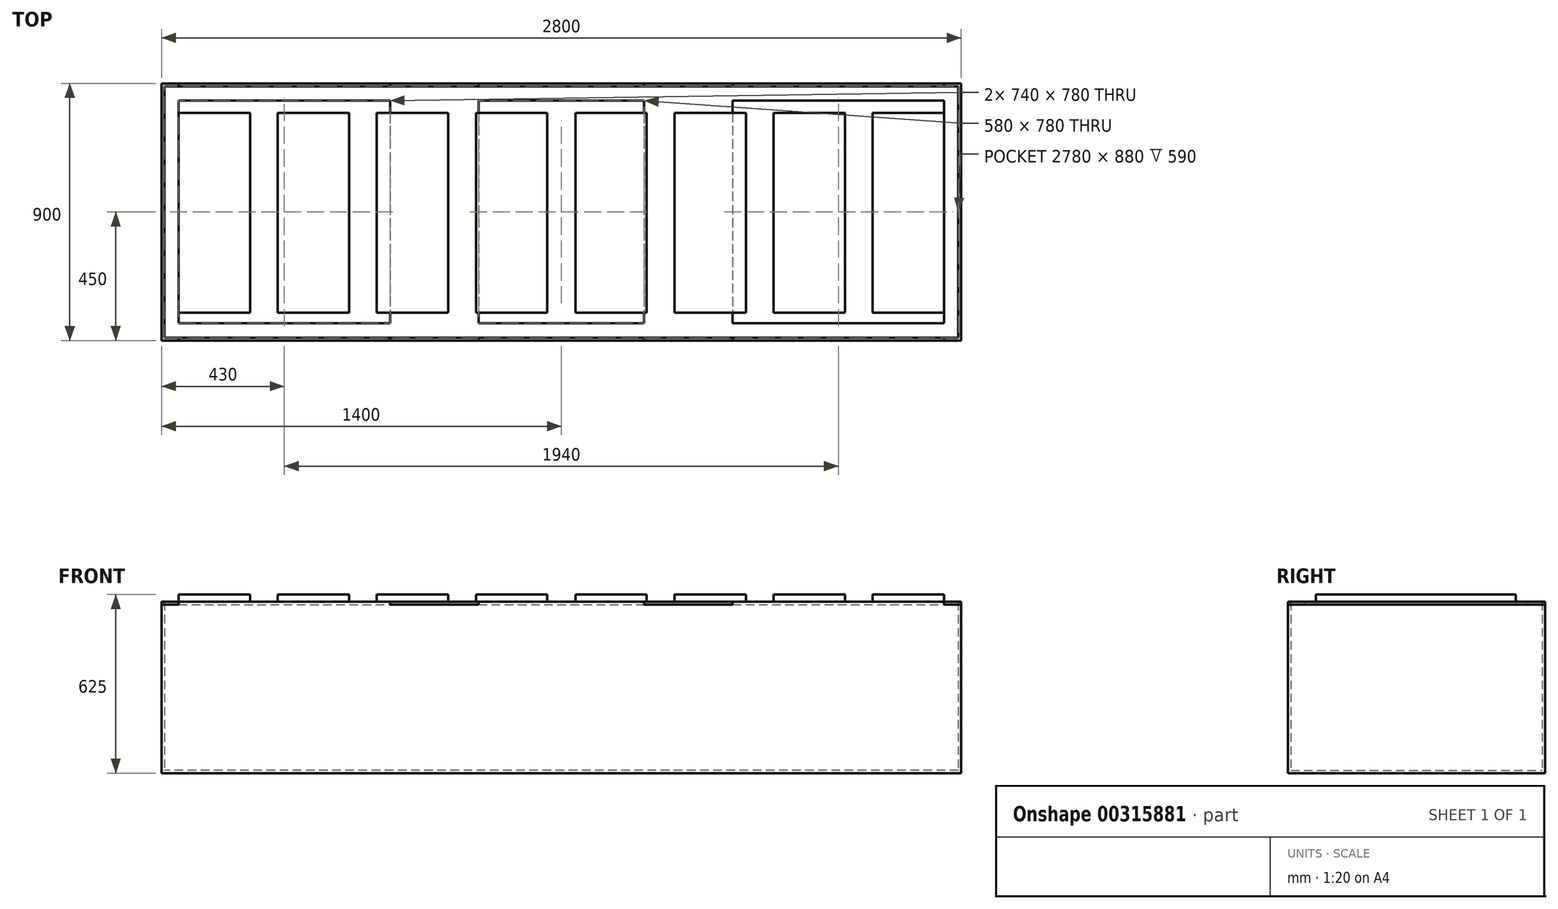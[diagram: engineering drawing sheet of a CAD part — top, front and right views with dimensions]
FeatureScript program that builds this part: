
annotation { "Feature Type Name" : "Feature", "Feature Type Description" : "" }
export const myFeature = defineFeature(function(context is Context, id is Id, definition is map)
    precondition{}
    {
        {
            var Q0;
            Q0=qCreatedBy(makeId("Top.planeOp"),FACE);
            var sketch = newSketch(context, id + "F0", { "sketchPlane" : qUnion([Q0])});
            skLineSegment(sketch, "E0.bottom", {"start": v(-1400, 450) * mm, "end": v(1400, 450) * mm});
            skLineSegment(sketch, "E0.top", {"start": v(-1400, -450) * mm, "end": v(1400, -450) * mm});
            skLineSegment(sketch, "E0.left", {"start": v(-1400, 450) * mm, "end": v(-1400, -450) * mm});
            skLineSegment(sketch, "E0.right", {"start": v(1400, 450) * mm, "end": v(1400, -450) * mm});
            skPoint(sketch, "E0.middle", {"position": v(0, 0) * mm});
            skLineSegment(sketch, "E1.bottom", {"start": v(-1390, 440) * mm, "end": v(1390, 440) * mm});
            skLineSegment(sketch, "E1.top", {"start": v(-1390, -440) * mm, "end": v(1390, -440) * mm});
            skLineSegment(sketch, "E1.left", {"start": v(-1390, 440) * mm, "end": v(-1390, -440) * mm});
            skLineSegment(sketch, "E1.right", {"start": v(1390, 440) * mm, "end": v(1390, -440) * mm});
            skSolve(sketch);
        }
        {
            var Q0;
            Q0=qSketchRegion(id+"F0",true);
            extrude(context, id + "F1", {"entities" : qUnion([Q0]), "depth" : 600 * mm});
        }
        {
            var Q0;
            Q0=makeQuery(id+"F1.opExtrude","CAP_FACE",FACE,{"disambiguationData":[OSD([sQuery(id+"F0.wireOp",EDGE,"E0.bottom"),sQuery(id+"F0.wireOp",EDGE,"E0.top"),sQuery(id+"F0.wireOp",EDGE,"E0.left"),sQuery(id+"F0.wireOp",EDGE,"E0.right"),sQuery(id+"F0.wireOp",EDGE,"E1.bottom"),sQuery(id+"F0.wireOp",EDGE,"E1.top"),sQuery(id+"F0.wireOp",EDGE,"E1.left"),sQuery(id+"F0.wireOp",EDGE,"E1.right")])],"isStart":true});
            var sketch = newSketch(context, id + "F2", { "sketchPlane" : qUnion([Q0])});
            skLineSegment(sketch, "E2.bottom", {"start": v(-1400, -450) * mm, "end": v(1400, -450) * mm});
            skLineSegment(sketch, "E2.top", {"start": v(-1400, 450) * mm, "end": v(1400, 450) * mm});
            skLineSegment(sketch, "E2.left", {"start": v(-1400, -450) * mm, "end": v(-1400, 450) * mm});
            skLineSegment(sketch, "E2.right", {"start": v(1400, -450) * mm, "end": v(1400, 450) * mm});
            skPoint(sketch, "E2.middle", {"position": v(0, 0) * mm});
            skSolve(sketch);
        }
        {
            var Q0;
            Q0=qSketchRegion(id+"F2",true);
            extrude(context, id + "F3", {"entities" : qUnion([Q0]), "operationType" : NewBodyOperationType.ADD, "oppositeDirection" : true, "depth" : 10 * mm});
        }
        {
            var Q0;
            Q0=makeQuery(id+"F1.opExtrude","CAP_FACE",FACE,{"disambiguationData":[OSD([sQuery(id+"F0.wireOp",EDGE,"E0.bottom"),sQuery(id+"F0.wireOp",EDGE,"E0.top"),sQuery(id+"F0.wireOp",EDGE,"E0.left"),sQuery(id+"F0.wireOp",EDGE,"E0.right"),sQuery(id+"F0.wireOp",EDGE,"E1.bottom"),sQuery(id+"F0.wireOp",EDGE,"E1.top"),sQuery(id+"F0.wireOp",EDGE,"E1.left"),sQuery(id+"F0.wireOp",EDGE,"E1.right")])],"isStart":false});
            var sketch = newSketch(context, id + "F4", { "sketchPlane" : qUnion([Q0])});
            skLineSegment(sketch, "E3.bottom", {"start": v(-1400, -450) * mm, "end": v(-1340, -450) * mm});
            skLineSegment(sketch, "E3.top", {"start": v(-1400, 450) * mm, "end": v(-1340, 450) * mm});
            skLineSegment(sketch, "E3.left", {"start": v(-1400, -450) * mm, "end": v(-1400, 450) * mm});
            skLineSegment(sketch, "E3.right", {"start": v(-1340, -450) * mm, "end": v(-1340, -440) * mm});
            skLineSegment(sketch, "E4.bottom", {"start": v(-600, 450) * mm, "end": v(-290, 450) * mm});
            skLineSegment(sketch, "E4.top", {"start": v(-600, -450) * mm, "end": v(-290, -450) * mm});
            skLineSegment(sketch, "E4.left", {"start": v(-600, 450) * mm, "end": v(-600, 440) * mm});
            skLineSegment(sketch, "E4.right", {"start": v(-290, 450) * mm, "end": v(-290, 440) * mm});
            skLineSegment(sketch, "E5", {"start": v(0, 0) * mm, "end": v(0, 217.45) * mm, "construction": true});
            skLineSegment(sketch, "E6.MirrorCS", {"start": v(600, 450) * mm, "end": v(600, 440) * mm});
            skLineSegment(sketch, "E7.MirrorCS", {"start": v(600, -450) * mm, "end": v(290, -450) * mm});
            skLineSegment(sketch, "E8.MirrorCS", {"start": v(600, 450) * mm, "end": v(290, 450) * mm});
            skLineSegment(sketch, "E9.MirrorCS", {"start": v(290, 450) * mm, "end": v(290, 440) * mm});
            skLineSegment(sketch, "E10.MirrorCS", {"start": v(1400, -450) * mm, "end": v(1340, -450) * mm});
            skLineSegment(sketch, "E11.MirrorCS", {"start": v(1400, 450) * mm, "end": v(1340, 450) * mm});
            skLineSegment(sketch, "E12.MirrorCS", {"start": v(1400, -450) * mm, "end": v(1400, 450) * mm});
            skLineSegment(sketch, "E13.MirrorCS", {"start": v(1340, -450) * mm, "end": v(1340, -440) * mm});
            skLineSegment(sketch, "E14.bottom", {"start": v(-1390, 440) * mm, "end": v(1400, 440) * mm});
            skLineSegment(sketch, "E14.top", {"start": v(-1340, 390) * mm, "end": v(-600, 390) * mm});
            skLineSegment(sketch, "E14.left", {"start": v(-1390, 440) * mm, "end": v(-1390, 390) * mm});
            skLineSegment(sketch, "E14.right", {"start": v(1400, 440) * mm, "end": v(1400, 390) * mm});
            skLineSegment(sketch, "E15", {"start": v(0, 0) * mm, "end": v(194.9, 0) * mm, "construction": true});
            skLineSegment(sketch, "E16.MirrorCS", {"start": v(1400, -440) * mm, "end": v(1400, -390) * mm});
            skLineSegment(sketch, "E17.MirrorCS", {"start": v(-1390, -440) * mm, "end": v(-1390, -390) * mm});
            skLineSegment(sketch, "E18.MirrorCS", {"start": v(-1340, -390) * mm, "end": v(-600, -390) * mm});
            skLineSegment(sketch, "E19.MirrorCS", {"start": v(-1390, -440) * mm, "end": v(1400, -440) * mm});
            skLineSegment(sketch, "E20.trimOffspring", {"start": v(-290, 390) * mm, "end": v(290, 390) * mm});
            skLineSegment(sketch, "E21.trimOffspring", {"start": v(-290, -390) * mm, "end": v(290, -390) * mm});
            skLineSegment(sketch, "E22.trimOffspring", {"start": v(600, -390) * mm, "end": v(1340, -390) * mm});
            skLineSegment(sketch, "E23.trimOffspring", {"start": v(600, 390) * mm, "end": v(1340, 390) * mm});
            skLineSegment(sketch, "E24.trimOffspring", {"start": v(-1340, 440) * mm, "end": v(-1340, 450) * mm});
            skLineSegment(sketch, "E25.trimOffspring", {"start": v(-1340, -390) * mm, "end": v(-1340, 390) * mm});
            skLineSegment(sketch, "E26.trimOffspring", {"start": v(-600, 390) * mm, "end": v(-600, -390) * mm});
            skLineSegment(sketch, "E27.trimOffspring", {"start": v(-600, -440) * mm, "end": v(-600, -450) * mm});
            skLineSegment(sketch, "E28.trimOffspring", {"start": v(-290, -440) * mm, "end": v(-290, -450) * mm});
            skLineSegment(sketch, "E29.trimOffspring", {"start": v(-290, 390) * mm, "end": v(-290, -390) * mm});
            skLineSegment(sketch, "E30.trimOffspring", {"start": v(290, 390) * mm, "end": v(290, -390) * mm});
            skLineSegment(sketch, "E31.trimOffspring", {"start": v(600, 390) * mm, "end": v(600, -390) * mm});
            skLineSegment(sketch, "E32.trimOffspring", {"start": v(290, -440) * mm, "end": v(290, -450) * mm});
            skLineSegment(sketch, "E33.trimOffspring", {"start": v(600, -440) * mm, "end": v(600, -450) * mm});
            skLineSegment(sketch, "E34.trimOffspring", {"start": v(1340, 440) * mm, "end": v(1340, 450) * mm});
            skLineSegment(sketch, "E35.trimOffspring", {"start": v(1340, -390) * mm, "end": v(1340, 390) * mm});
            skSolve(sketch);
        }
        {
            var Q0;
            Q0=qSketchRegion(id+"F4",true);
            extrude(context, id + "F5", {"entities" : qUnion([Q0]), "oppositeDirection" : true, "depth" : 10 * mm});
        }
        {
            var Q0;
            Q0=makeQuery(id+"F5.opExtrude","CAP_FACE",FACE,{"disambiguationData":[OSD([sQuery(id+"F4.wireOp",EDGE,"E3.top"),sQuery(id+"F4.wireOp",EDGE,"E3.left"),sQuery(id+"F4.wireOp",EDGE,"E3.right"),sQuery(id+"F4.wireOp",EDGE,"E4.bottom"),sQuery(id+"F4.wireOp",EDGE,"E4.left"),sQuery(id+"F4.wireOp",EDGE,"E4.right"),sQuery(id+"F4.wireOp",EDGE,"E6.MirrorCS"),sQuery(id+"F4.wireOp",EDGE,"E8.MirrorCS"),sQuery(id+"F4.wireOp",EDGE,"E9.MirrorCS"),sQuery(id+"F4.wireOp",EDGE,"E11.MirrorCS"),sQuery(id+"F4.wireOp",EDGE,"E12.MirrorCS"),sQuery(id+"F4.wireOp",EDGE,"E13.MirrorCS"),sQuery(id+"F4.wireOp",EDGE,"E14.bottom"),sQuery(id+"F4.wireOp",EDGE,"E14.top"),sQuery(id+"F4.wireOp",EDGE,"E14.right"),sQuery(id+"F4.wireOp",EDGE,"E10.MirrorCS"),sQuery(id+"F4.wireOp",EDGE,"E16.MirrorCS"),sQuery(id+"F4.wireOp",EDGE,"E3.bottom"),sQuery(id+"F4.wireOp",EDGE,"E7.MirrorCS"),sQuery(id+"F4.wireOp",EDGE,"E18.MirrorCS"),sQuery(id+"F4.wireOp",EDGE,"E19.MirrorCS"),sQuery(id+"F4.wireOp",EDGE,"E4.top"),sQuery(id+"F4.wireOp",EDGE,"E20.trimOffspring"),sQuery(id+"F4.wireOp",EDGE,"E21.trimOffspring"),sQuery(id+"F4.wireOp",EDGE,"E22.trimOffspring"),sQuery(id+"F4.wireOp",EDGE,"E23.trimOffspring"),sQuery(id+"F4.wireOp",EDGE,"E24.trimOffspring"),sQuery(id+"F4.wireOp",EDGE,"E25.trimOffspring"),sQuery(id+"F4.wireOp",EDGE,"E26.trimOffspring"),sQuery(id+"F4.wireOp",EDGE,"E27.trimOffspring"),sQuery(id+"F4.wireOp",EDGE,"E28.trimOffspring"),sQuery(id+"F4.wireOp",EDGE,"E29.trimOffspring"),sQuery(id+"F4.wireOp",EDGE,"E30.trimOffspring"),sQuery(id+"F4.wireOp",EDGE,"E31.trimOffspring"),sQuery(id+"F4.wireOp",EDGE,"E32.trimOffspring"),sQuery(id+"F4.wireOp",EDGE,"E33.trimOffspring"),sQuery(id+"F4.wireOp",EDGE,"E34.trimOffspring"),sQuery(id+"F4.wireOp",EDGE,"E35.trimOffspring")])],"isStart":true});
            var sketch = newSketch(context, id + "F6", { "sketchPlane" : qUnion([Q0])});
            skLineSegment(sketch, "E36", {"start": v(0, 0) * mm, "end": v(0, 730.29) * mm, "construction": true});
            skPoint(sketch, "E36.endSnap0", {"position": v(0, 390) * mm});
            skLineSegment(sketch, "E37.bottom", {"start": v(-1340, 347.13) * mm, "end": v(-1090, 347.13) * mm});
            skLineSegment(sketch, "E37.top", {"start": v(-1340, -352.87) * mm, "end": v(-1090, -352.87) * mm});
            skLineSegment(sketch, "E37.left", {"start": v(-1340, 347.13) * mm, "end": v(-1340, -352.87) * mm});
            skLineSegment(sketch, "E37.right", {"start": v(-1090, 347.13) * mm, "end": v(-1090, -352.87) * mm});
            skLineSegment(sketch, "E38.bottom", {"start": v(-993, 347.13) * mm, "end": v(-743, 347.13) * mm});
            skLineSegment(sketch, "E38.top", {"start": v(-993, -352.87) * mm, "end": v(-743, -352.87) * mm});
            skLineSegment(sketch, "E38.left", {"start": v(-993, 347.13) * mm, "end": v(-993, -352.87) * mm});
            skLineSegment(sketch, "E38.right", {"start": v(-743, 347.13) * mm, "end": v(-743, -352.87) * mm});
            skLineSegment(sketch, "E39.bottom", {"start": v(-646, 347.13) * mm, "end": v(-396, 347.13) * mm});
            skLineSegment(sketch, "E39.top", {"start": v(-646, -352.87) * mm, "end": v(-396, -352.87) * mm});
            skLineSegment(sketch, "E39.left", {"start": v(-646, 347.13) * mm, "end": v(-646, -352.87) * mm});
            skLineSegment(sketch, "E39.right", {"start": v(-396, 347.13) * mm, "end": v(-396, -352.87) * mm});
            skLineSegment(sketch, "E40.bottom", {"start": v(-299, 347.13) * mm, "end": v(-49, 347.13) * mm});
            skLineSegment(sketch, "E40.top", {"start": v(-299, -352.87) * mm, "end": v(-49, -352.87) * mm});
            skLineSegment(sketch, "E40.left", {"start": v(-299, 347.13) * mm, "end": v(-299, -352.87) * mm});
            skLineSegment(sketch, "E40.right", {"start": v(-49, 347.13) * mm, "end": v(-49, -352.87) * mm});
            skLineSegment(sketch, "E41.MirrorCS", {"start": v(299, 347.13) * mm, "end": v(299, -352.87) * mm});
            skLineSegment(sketch, "E42.MirrorCS", {"start": v(743, 347.13) * mm, "end": v(743, -352.87) * mm});
            skLineSegment(sketch, "E43.MirrorCS", {"start": v(993, 347.13) * mm, "end": v(993, -352.87) * mm});
            skLineSegment(sketch, "E44.MirrorCS", {"start": v(993, -352.87) * mm, "end": v(743, -352.87) * mm});
            skLineSegment(sketch, "E45.MirrorCS", {"start": v(993, 347.13) * mm, "end": v(743, 347.13) * mm});
            skLineSegment(sketch, "E46.MirrorCS", {"start": v(396, 347.13) * mm, "end": v(396, -352.87) * mm});
            skLineSegment(sketch, "E47.MirrorCS", {"start": v(49, 347.13) * mm, "end": v(49, -352.87) * mm});
            skLineSegment(sketch, "E48.MirrorCS", {"start": v(1090, 347.13) * mm, "end": v(1090, -352.87) * mm});
            skLineSegment(sketch, "E49.MirrorCS", {"start": v(1340, 347.13) * mm, "end": v(1340, -352.87) * mm});
            skLineSegment(sketch, "E50.MirrorCS", {"start": v(1340, -352.87) * mm, "end": v(1090, -352.87) * mm});
            skLineSegment(sketch, "E51.MirrorCS", {"start": v(1340, 347.13) * mm, "end": v(1090, 347.13) * mm});
            skLineSegment(sketch, "E52.MirrorCS", {"start": v(646, 347.13) * mm, "end": v(646, -352.87) * mm});
            skLineSegment(sketch, "E53.MirrorCS", {"start": v(646, -352.87) * mm, "end": v(396, -352.87) * mm});
            skLineSegment(sketch, "E54.MirrorCS", {"start": v(646, 347.13) * mm, "end": v(396, 347.13) * mm});
            skLineSegment(sketch, "E55.MirrorCS", {"start": v(299, 347.13) * mm, "end": v(49, 347.13) * mm});
            skLineSegment(sketch, "E56.MirrorCS", {"start": v(299, -352.87) * mm, "end": v(49, -352.87) * mm});
            skSolve(sketch);
        }
        {
            var Q0;
            Q0 = qSketchRegion(id + "F6", true);
            extrude(context, id + "F7", {"entities" : qUnion([Q0]), "depth" : 25 * mm});
        }
    });
